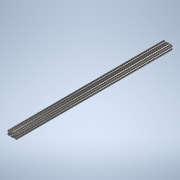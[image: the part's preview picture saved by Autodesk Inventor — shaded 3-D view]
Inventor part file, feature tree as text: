
AUTODESK INVENTOR PART (.ipt)
format: ipt  version: 2020 (Build 240168000, 168)  size: 362,496 bytes
history: native  units: in
note: dims shown in document units (in); Inventor stores cm internally (conversion verified against a paired STEP export)
features: sketch x2, extrude x1
ambient origin geometry x8: Origin, YZ Plane, XZ Plane, XY Plane, X Axis, Y Axis, Z Axis, Center Point
bodies: Solid1 (feature_tree)
feature tree (3):
  extrude  "Extrusion1"  [1 undecoded]
  sketch  "Sketch2"
  sketch  "Sketch1"  dims[d0=35.0in d1=0.0in]
note: 1 required parameter value undecoded (feature->parameter linkage not recoverable at this tier; creation-order binding heuristic only, values carry confidence <= 0.55)
